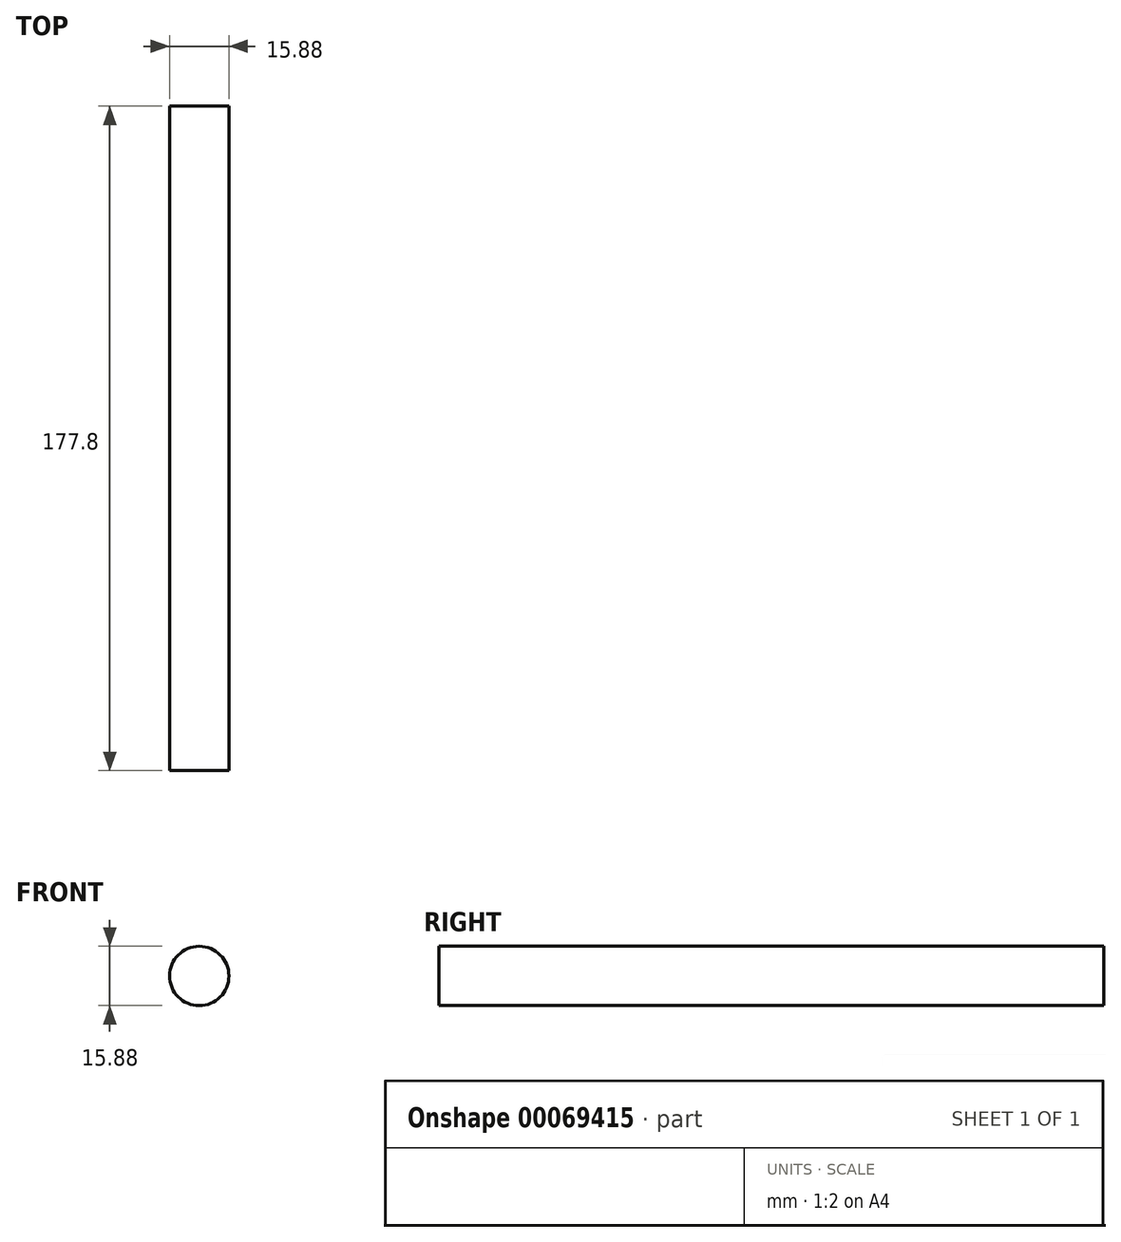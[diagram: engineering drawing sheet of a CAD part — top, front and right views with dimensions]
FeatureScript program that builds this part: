
annotation { "Feature Type Name" : "Feature", "Feature Type Description" : "" }
export const myFeature = defineFeature(function(context is Context, id is Id, definition is map)
    precondition{}
    {
        {
            var Q0;
            Q0=qCreatedBy(makeId("Front.planeOp"),FACE);
            var sketch = newSketch(context, id + "F0", { "sketchPlane" : qUnion([Q0])});
            skCircle(sketch, "E0", {"center": v(0, 0) * mm, "radius": 7.94 * mm});
            skSolve(sketch);
        }
        {
            var Q0;
            Q0 = qSketchRegion(id + "F0", true);
            extrude(context, id + "F1", {"entities" : qUnion([Q0]), "depth" : 177.8 * mm});
        }
    });
